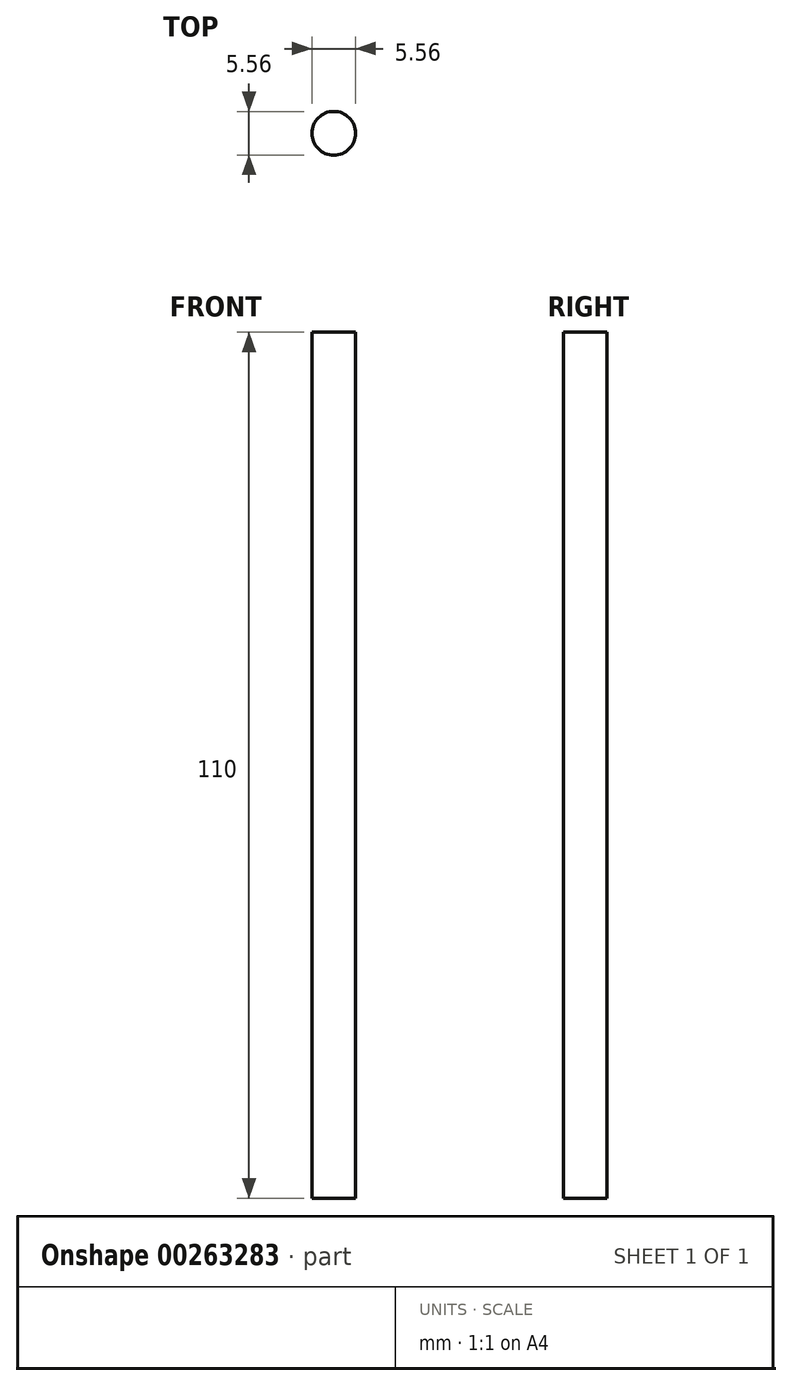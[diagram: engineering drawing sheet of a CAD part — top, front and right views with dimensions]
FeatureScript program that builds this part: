
annotation { "Feature Type Name" : "Feature", "Feature Type Description" : "" }
export const myFeature = defineFeature(function(context is Context, id is Id, definition is map)
    precondition{}
    {
        {
            var Q0;
            Q0=qCreatedBy(makeId("Top.planeOp"),FACE);
            var sketch = newSketch(context, id + "F0", { "sketchPlane" : qUnion([Q0])});
            skCircle(sketch, "E0", {"center": v(0, 0) * mm, "radius": 2.78 * mm});
            skSolve(sketch);
        }
        {
            var Q0;
            Q0 = qSketchRegion(id + "F0", true);
            extrude(context, id + "F1", {"entities" : qUnion([Q0]), "depth" : 110 * mm});
        }
    });
